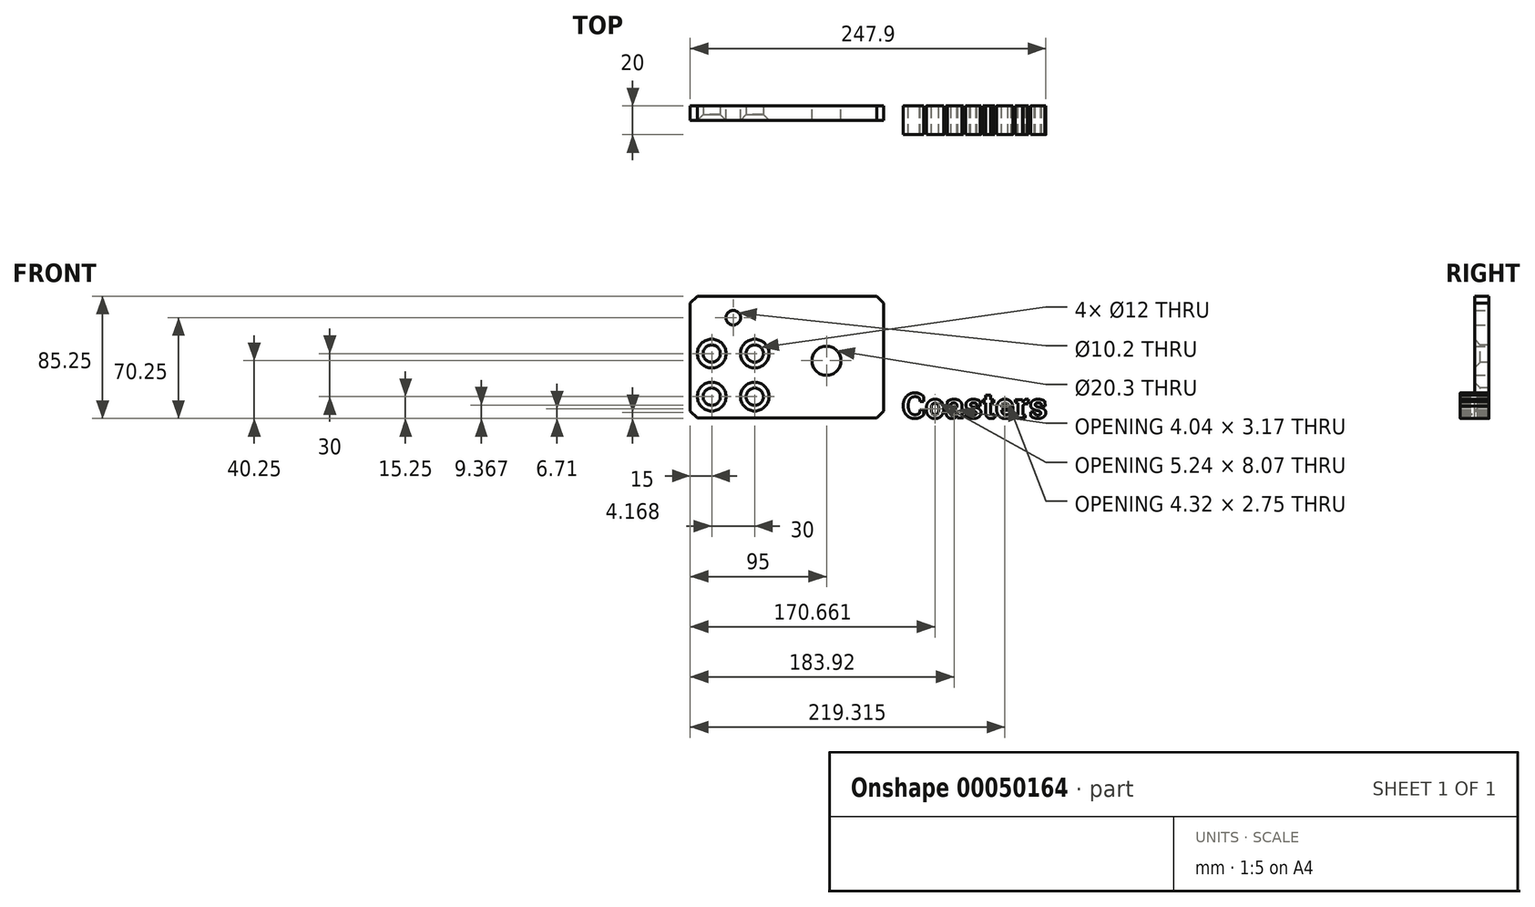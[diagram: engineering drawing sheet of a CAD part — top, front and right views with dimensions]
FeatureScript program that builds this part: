
annotation { "Feature Type Name" : "Feature", "Feature Type Description" : "" }
export const myFeature = defineFeature(function(context is Context, id is Id, definition is map)
    precondition{}
    {
        {
            var Q0;
            Q0=qCreatedBy(makeId("Front.planeOp"),FACE);
            var sketch = newSketch(context, id + "F0", { "sketchPlane" : qUnion([Q0])});
            skLineSegment(sketch, "E0.bottom", {"start": v(0, 0) * mm, "end": v(-135, 0) * mm});
            skLineSegment(sketch, "E0.top", {"start": v(0, 85) * mm, "end": v(-135, 85) * mm});
            skLineSegment(sketch, "E0.left", {"start": v(0, 0) * mm, "end": v(0, 85) * mm});
            skLineSegment(sketch, "E0.right", {"start": v(-135, 0) * mm, "end": v(-135, 85) * mm});
            skCircle(sketch, "E1", {"center": v(-105, 70) * mm, "radius": 5.1 * mm});
            skCircle(sketch, "E2", {"center": v(-40, 40) * mm, "radius": 10.15 * mm});
            skSolve(sketch);
        }
        {
            var Q0;
            Q0 = qSketchRegion(id + "F0", true);
            extrude(context, id + "F1", {"entities" : qUnion([Q0]), "depth" : 10 * mm});
        }
        {
            var Q0;
            Q0=makeQuery(id+"F1.opExtrude","CAP_FACE",FACE,{"disambiguationData":[OSD([sQuery(id+"F0.wireOp",EDGE,"E0.bottom"),sQuery(id+"F0.wireOp",EDGE,"E0.top"),sQuery(id+"F0.wireOp",EDGE,"E0.left"),sQuery(id+"F0.wireOp",EDGE,"E0.right"),sQuery(id+"F0.wireOp",EDGE,"E1"),sQuery(id+"F0.wireOp",EDGE,"E2")])],"isStart":false});
            var sketch = newSketch(context, id + "F2", { "sketchPlane" : qUnion([Q0])});
            skPoint(sketch, "E3", {"position": v(-120, 15) * mm});
            skPoint(sketch, "E4.0.1.0", {"position": v(-120, 45) * mm});
            skPoint(sketch, "E4.1.0.0", {"position": v(-90, 15) * mm});
            skPoint(sketch, "E4.1.1.0", {"position": v(-90, 45) * mm});
            skLineSegment(sketch, "E4.direction1", {"start": v(-120, 15) * mm, "end": v(-90, 15) * mm, "construction": true});
            skLineSegment(sketch, "E4.direction2", {"start": v(-120, 15) * mm, "end": v(-120, 45) * mm, "construction": true});
            skSolve(sketch);
        }
        {
            var Q0;
            Q0=sQuery(id+"F2.wireOp",VERTEX,"E4.0.1.0");
            var Q1;
            Q1=sQuery(id+"F2.wireOp",VERTEX,"E4.1.1.0");
            var Q2;
            Q2=sQuery(id+"F2.wireOp",VERTEX,"E4.1.0.0");
            var Q3;
            Q3=sQuery(id+"F2.wireOp",VERTEX,"E3");
            var Q4;
            Q4=makeQuery(id+"F1.opExtrude","SWEPT_BODY",BODY,{"disambiguationData":[OSD([sQuery(id+"F0.wireOp",EDGE,"E0.bottom"),sQuery(id+"F0.wireOp",EDGE,"E0.top"),sQuery(id+"F0.wireOp",EDGE,"E0.left"),sQuery(id+"F0.wireOp",EDGE,"E0.right"),sQuery(id+"F0.wireOp",EDGE,"E1"),sQuery(id+"F0.wireOp",EDGE,"E2")])]});
            hole(context, id + "F3", {"style" : HoleStyle.C_SINK, "holeDiameter" : 12 * mm, "cSinkDiameter" : 20 * mm, "endStyle" : HoleEndStyle.THROUGH, "locations" : qUnion([Q0, Q1, Q2, Q3]), "scope" : qUnion([Q4]), "cSinkAngle" : 90 * degree});
        }
        {
            var Q0;
            Q0=makeQuery(id+"F1.opExtrude","SWEPT_EDGE",EDGE,{"disambiguationData":[OSD([sQuery(id+"F0.wireOp",EDGE,"E0.top"),sQuery(id+"F0.wireOp",EDGE,"E0.right")])]});
            var Q1;
            Q1=makeQuery(id+"F1.opExtrude","SWEPT_EDGE",EDGE,{"disambiguationData":[OSD([sQuery(id+"F0.wireOp",EDGE,"E0.top"),sQuery(id+"F0.wireOp",EDGE,"E0.left")])]});
            var Q2;
            Q2=makeQuery(id+"F1.opExtrude","SWEPT_EDGE",EDGE,{"disambiguationData":[OSD([sQuery(id+"F0.wireOp",EDGE,"E0.bottom"),sQuery(id+"F0.wireOp",EDGE,"E0.left")])]});
            var Q3;
            Q3=makeQuery(id+"F1.opExtrude","SWEPT_EDGE",EDGE,{"disambiguationData":[OSD([sQuery(id+"F0.wireOp",EDGE,"E0.bottom"),sQuery(id+"F0.wireOp",EDGE,"E0.right")])]});
            chamfer(context, id + "F4", {"entities" : qUnion([Q0, Q1, Q2, Q3]), "width" : 5 * mm, "tangentPropagation" : true});
        }
        {
            var Q0;
            Q0=qCreatedBy(makeId("Front.planeOp"),FACE);
            var sketch = newSketch(context, id + "F5", { "sketchPlane" : qUnion([Q0])});
            skText(sketch, "E5", { "text": "Coasters", "fontName": "RobotoSlab-Bold.ttf"});
            const initialGuessF5  = {"E5": [0.01292, 0, 1, 0, 0.01764]};
            skSetInitialGuess(sketch, initialGuessF5);
            skSolve(sketch);
        }
        {
            var Q0;
            Q0 = qSketchRegion(id + "F5", true);
            extrude(context, id + "F6", {"entities" : qUnion([Q0]), "depth" : 20 * mm});
        }
    });
